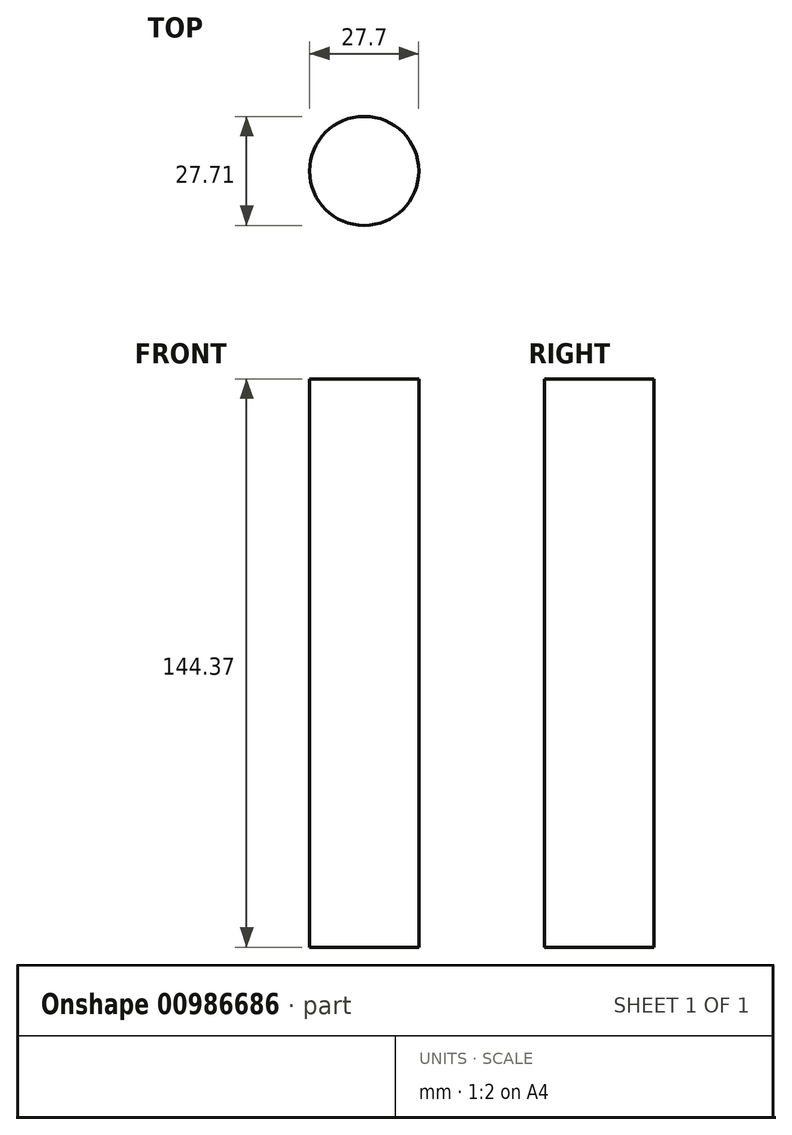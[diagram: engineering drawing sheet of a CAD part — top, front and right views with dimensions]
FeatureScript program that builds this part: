
annotation { "Feature Type Name" : "Feature", "Feature Type Description" : "" }
export const myFeature = defineFeature(function(context is Context, id is Id, definition is map)
    precondition{}
    {
        {
            var Q0;
            Q0=qCreatedBy(makeId("Top.planeOp"),FACE);
            var sketch = newSketch(context, id + "F0", { "sketchPlane" : qUnion([Q0])});
            skCircle(sketch, "E0", {"center": v(0, 11.6) * mm, "radius": 13.85 * mm});
            skSolve(sketch);
        }
        {
            var Q0;
            Q0 = qSketchRegion(id + "F0", true);
            extrude(context, id + "F1", {"entities" : qUnion([Q0]), "depth" : 144.37 * mm, "offsetDistance" : 25.4 * mm});
        }
    });
